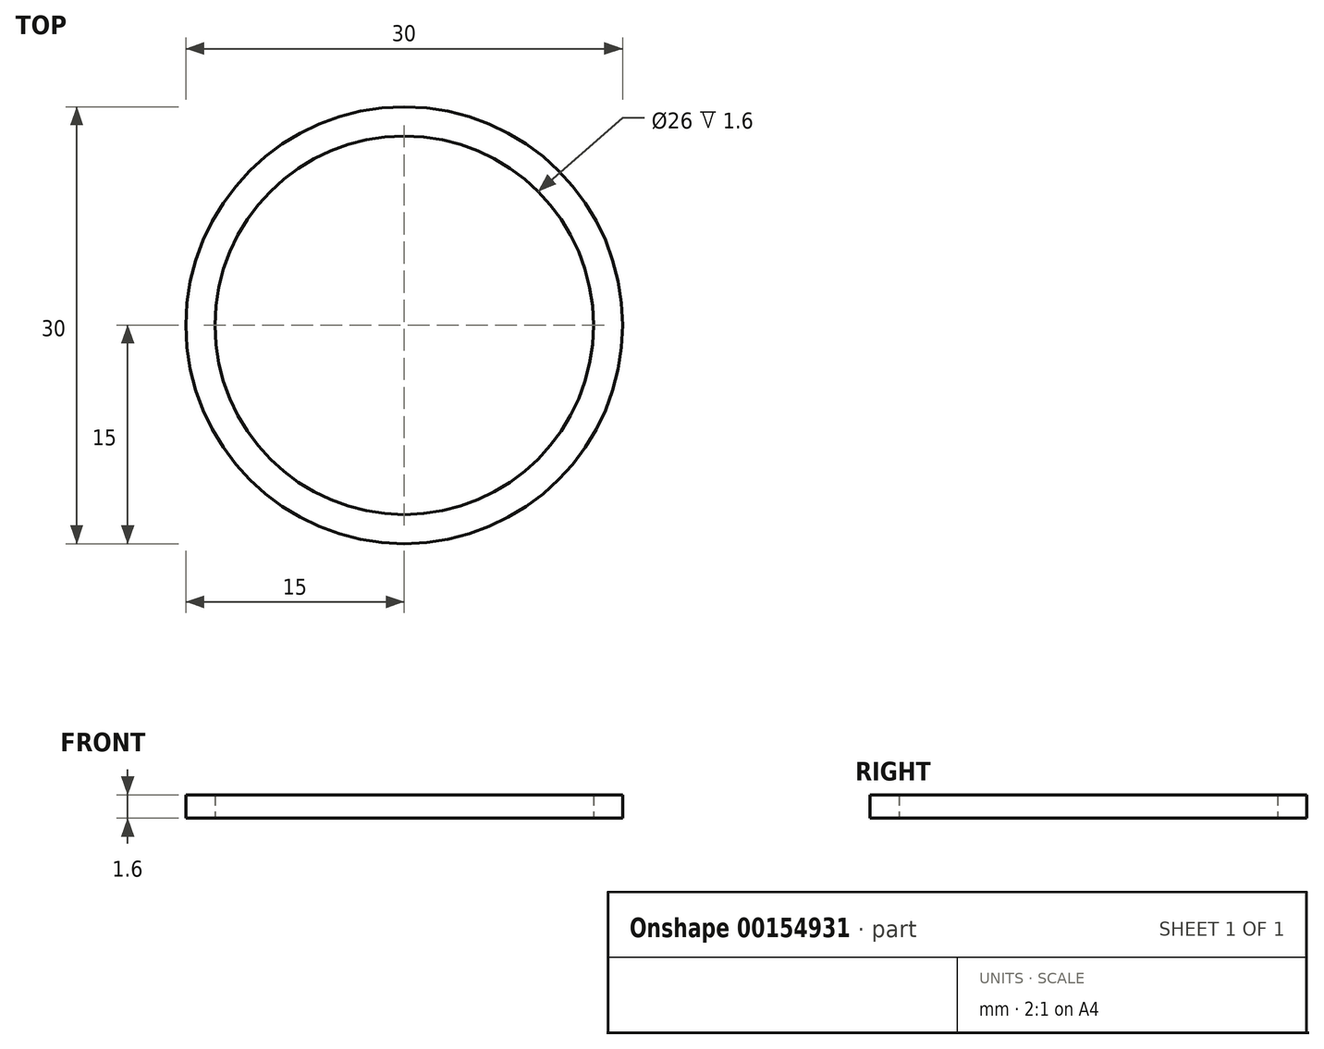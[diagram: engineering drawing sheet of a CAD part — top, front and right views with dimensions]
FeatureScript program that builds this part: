
annotation { "Feature Type Name" : "Feature", "Feature Type Description" : "" }
export const myFeature = defineFeature(function(context is Context, id is Id, definition is map)
    precondition{}
    {
        {
            var Q0;
            Q0=qCreatedBy(makeId("Top.planeOp"),FACE);
            var sketch = newSketch(context, id + "F0", { "sketchPlane" : qUnion([Q0])});
            skCircle(sketch, "E0", {"center": v(0, 0) * mm, "radius": 13 * mm});
            skCircle(sketch, "E1", {"center": v(0, 0) * mm, "radius": 15 * mm});
            skSolve(sketch);
        }
        {
            var Q0;
            Q0=makeQuery(id+"F0.imprint","IMPRINT",FACE,{"disambiguationData":[TD([[makeQuery(id+"F0.imprint","IMPRINT",EDGE,{"derivedFrom":sQuery(id+"F0.wireOp",EDGE,"E0")}),-1.0]])]});
            extrude(context, id + "F1", {"entities" : qUnion([Q0]), "depth" : 1.6 * mm});
        }
    });
